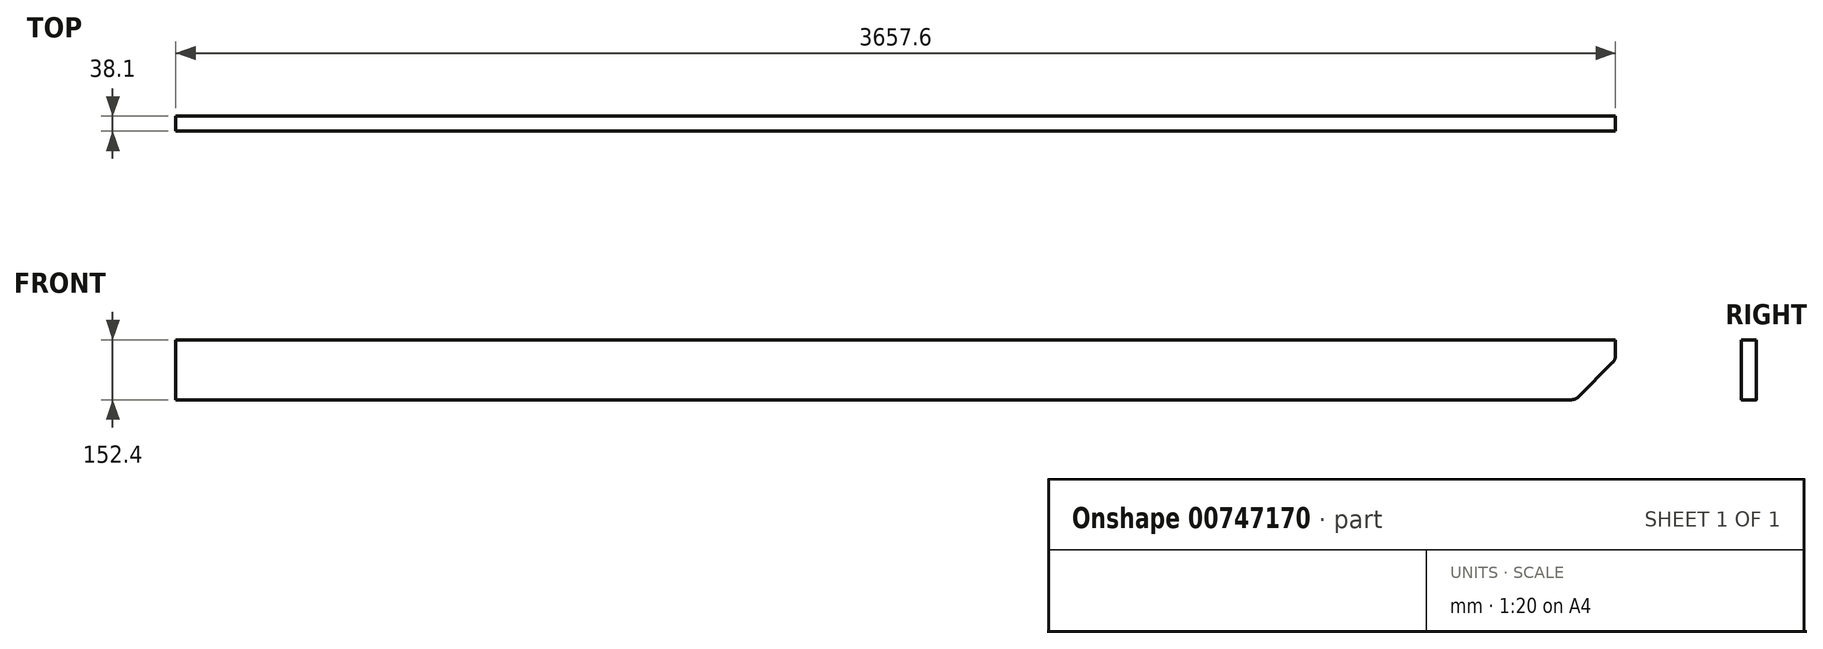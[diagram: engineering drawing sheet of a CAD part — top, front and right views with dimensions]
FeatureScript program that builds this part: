
annotation { "Feature Type Name" : "Feature", "Feature Type Description" : "" }
export const myFeature = defineFeature(function(context is Context, id is Id, definition is map)
    precondition{}
    {
        {
            var Q0;
            Q0=qCreatedBy(makeId("Right.planeOp"),FACE);
            var sketch = newSketch(context, id + "F0", { "sketchPlane" : qUnion([Q0])});
            skLineSegment(sketch, "E0.bottom", {"start": v(-47.44, 113.91) * mm, "end": v(-9.34, 113.91) * mm});
            skLineSegment(sketch, "E0.top", {"start": v(-47.44, -38.49) * mm, "end": v(-9.34, -38.49) * mm});
            skLineSegment(sketch, "E0.left", {"start": v(-47.44, 113.91) * mm, "end": v(-47.44, -38.49) * mm});
            skLineSegment(sketch, "E0.right", {"start": v(-9.34, 113.91) * mm, "end": v(-9.34, -38.49) * mm});
            skSolve(sketch);
        }
        {
            var Q0;
            Q0 = qSketchRegion(id + "F0", true);
            extrude(context, id + "F1", {"entities" : qUnion([Q0]), "depth" : 3657.6 * mm, "offsetDistance" : 25.4 * mm});
        }
        {
            var Q0;
            Q0=makeQuery(id+"F1.opExtrude","CAP_EDGE",EDGE,{"disambiguationData":[OSD([sQuery(id+"F0.wireOp",EDGE,"E0.top")])],"isStart":false});
            chamfer(context, id + "F2", {"entities" : qUnion([Q0]), "width" : 101.6 * mm, "tangentPropagation" : true});
        }
        {
            var Q0;
            {var subQ0=sQuery(id+"F0.wireOp",EDGE,"E0.top");Q0=makeQuery(id+"F2.opChamfer","BLEND_EDGE",EDGE,{"blendedFrom":[makeQuery(id+"F1.opExtrude","CAP_EDGE",EDGE,{"disambiguationData":[OSD([subQ0])],"isStart":false}),makeQuery(id+"F1.opExtrude","CAP_FACE",FACE,{"disambiguationData":[OSD([sQuery(id+"F0.wireOp",EDGE,"E0.bottom"),subQ0,sQuery(id+"F0.wireOp",EDGE,"E0.left"),sQuery(id+"F0.wireOp",EDGE,"E0.right")])],"isStart":false})],"blendedInto":[makeQuery(id+"F1.opExtrude","CAP_FACE",FACE,{"disambiguationData":[OSD([sQuery(id+"F0.wireOp",EDGE,"E0.bottom"),subQ0,sQuery(id+"F0.wireOp",EDGE,"E0.left"),sQuery(id+"F0.wireOp",EDGE,"E0.right")])],"isStart":false})]});}
            var Q1;
            {var subQ0=sQuery(id+"F0.wireOp",EDGE,"E0.top");Q1=makeQuery(id+"F2.opChamfer","BLEND_EDGE",EDGE,{"blendedFrom":[makeQuery(id+"F1.opExtrude","CAP_EDGE",EDGE,{"disambiguationData":[OSD([subQ0])],"isStart":false}),makeQuery(id+"F1.opExtrude","SWEPT_FACE",FACE,{"disambiguationData":[OSD([subQ0])]})],"blendedInto":[makeQuery(id+"F1.opExtrude","SWEPT_FACE",FACE,{"disambiguationData":[OSD([subQ0])]})]});}
            fillet(context, id + "F3", {"entities" : qUnion([Q0, Q1]), "radius" : 25.4 * mm, "tangentPropagation" : true, "allowEdgeOverflow" : false});
        }
    });
